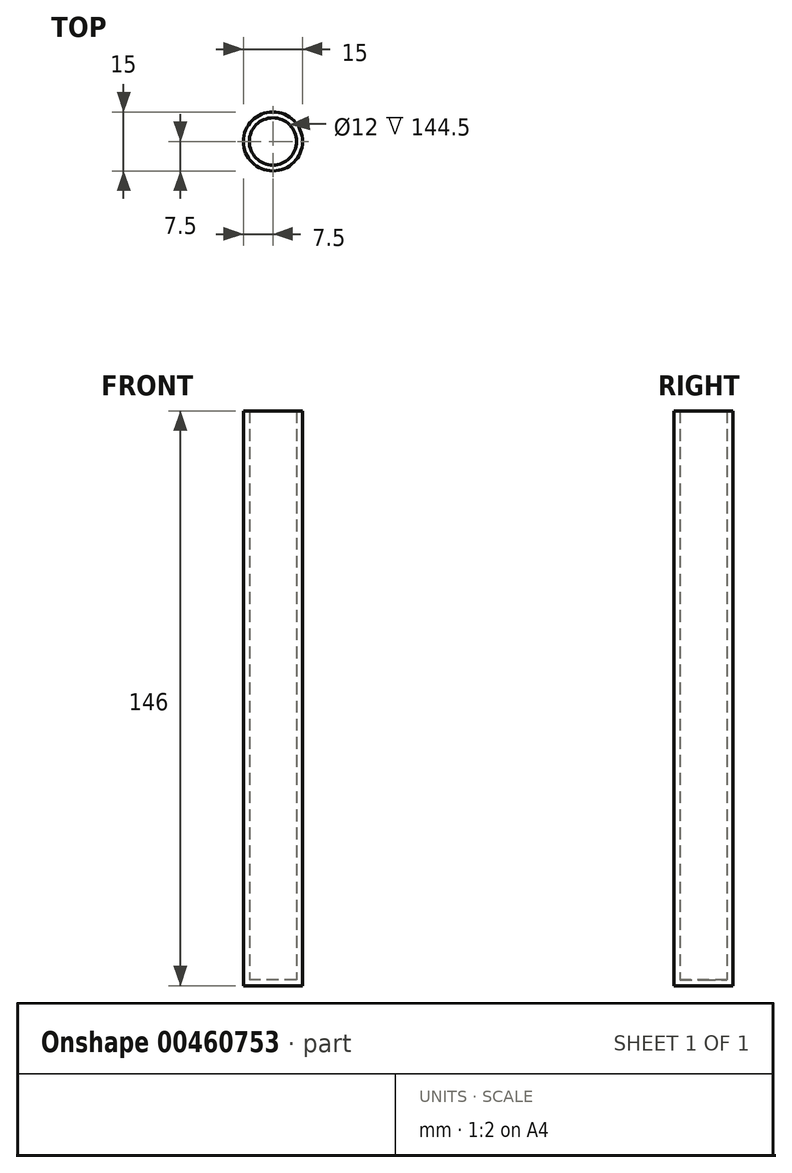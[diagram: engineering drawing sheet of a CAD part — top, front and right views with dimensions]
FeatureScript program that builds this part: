
annotation { "Feature Type Name" : "Feature", "Feature Type Description" : "" }
export const myFeature = defineFeature(function(context is Context, id is Id, definition is map)
    precondition{}
    {
        {
            var Q0;
            Q0=qCreatedBy(makeId("Top.planeOp"),FACE);
            var sketch = newSketch(context, id + "F0", { "sketchPlane" : qUnion([Q0])});
            skCircle(sketch, "E0", {"center": v(0, 0) * mm, "radius": 7.5 * mm});
            skSolve(sketch);
        }
        {
            var Q0;
            Q0=makeQuery(id+"F0.imprint","IMPRINT",FACE,{"disambiguationData":[TD([[makeQuery(id+"F0.imprint","IMPRINT",EDGE,{"derivedFrom":sQuery(id+"F0.wireOp",EDGE,"E0")}),1.0]])]});
            var Q1;
            Q1=sQuery(id+"F0.wireOp",EDGE,"E0");
            extrude(context, id + "F1", {"entities" : qUnion([Q0]), "surfaceEntities" : qUnion([Q1]), "depth" : 146 * mm, "offsetDistance" : 25 * mm});
        }
        {
            var Q0;
            Q0=makeQuery(id+"F1.opExtrude","CAP_FACE",FACE,{"disambiguationData":[OSD([sQuery(id+"F0.wireOp",EDGE,"E0")])],"isStart":false});
            shell(context, id + "F2", {"entities" : qUnion([Q0]), "thickness" : 1.5 * mm});
        }
    });
